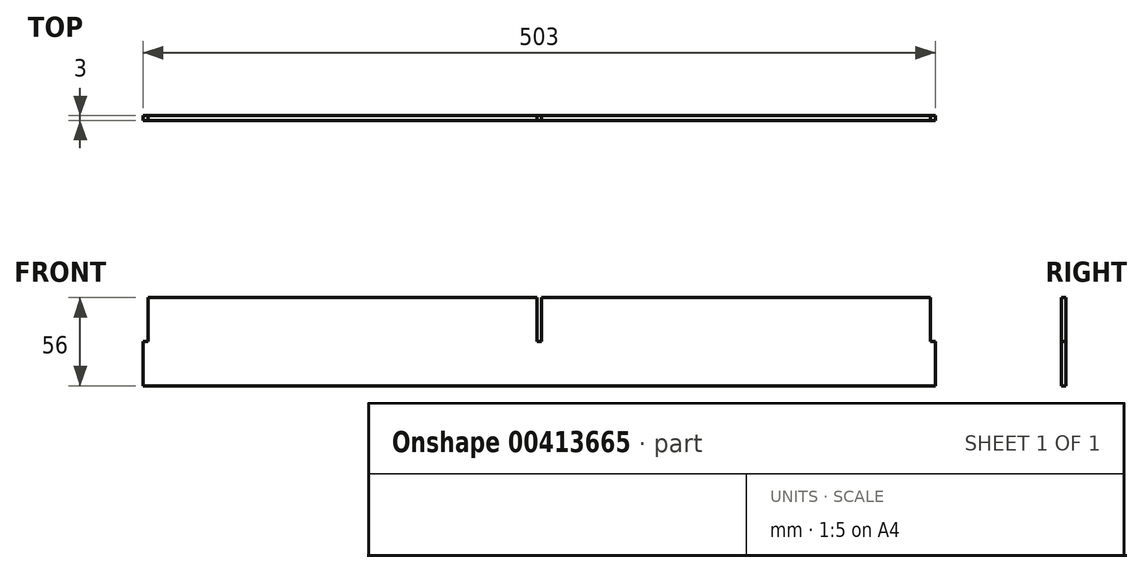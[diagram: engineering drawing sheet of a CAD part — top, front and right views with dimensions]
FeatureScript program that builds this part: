
annotation { "Feature Type Name" : "Feature", "Feature Type Description" : "" }
export const myFeature = defineFeature(function(context is Context, id is Id, definition is map)
    precondition{}
    {
        {
            var Q0;
            Q0=qCreatedBy(makeId("Front.planeOp"),FACE);
            var sketch = newSketch(context, id + "F0", { "sketchPlane" : qUnion([Q0])});
            skLineSegment(sketch, "E0.bottom", {"start": v(0, 0) * mm, "end": v(503, 0) * mm});
            skLineSegment(sketch, "E0.top", {"start": v(3, 56) * mm, "end": v(250, 56) * mm});
            skLineSegment(sketch, "E0.left", {"start": v(0, 0) * mm, "end": v(0, 28) * mm});
            skLineSegment(sketch, "E0.right", {"start": v(503, 0) * mm, "end": v(503, 28) * mm});
            skLineSegment(sketch, "E1.bottom", {"start": v(250, 28) * mm, "end": v(253, 28) * mm});
            skLineSegment(sketch, "E1.left", {"start": v(250, 28) * mm, "end": v(250, 56) * mm});
            skLineSegment(sketch, "E1.right", {"start": v(253, 28) * mm, "end": v(253, 56) * mm});
            skLineSegment(sketch, "E2.top", {"start": v(503, 28) * mm, "end": v(500, 28) * mm});
            skLineSegment(sketch, "E2.right", {"start": v(500, 56) * mm, "end": v(500, 28) * mm});
            skLineSegment(sketch, "E3.top", {"start": v(0, 28) * mm, "end": v(3, 28) * mm});
            skLineSegment(sketch, "E3.right", {"start": v(3, 56) * mm, "end": v(3, 28) * mm});
            skLineSegment(sketch, "E4.trimOffspring", {"start": v(253, 56) * mm, "end": v(500, 56) * mm});
            skSolve(sketch);
        }
        {
            var Q0;
            Q0=makeQuery(id+"F0.imprint","IMPRINT",FACE,{"disambiguationData":[TD([[makeQuery(id+"F0.imprint","IMPRINT",EDGE,{"derivedFrom":sQuery(id+"F0.wireOp",EDGE,"E0.bottom")}),1.0]])]});
            extrude(context, id + "F1", {"entities" : qUnion([Q0]), "endBound" : BoundingType.SYMMETRIC, "depth" : 3 * mm});
        }
    });
